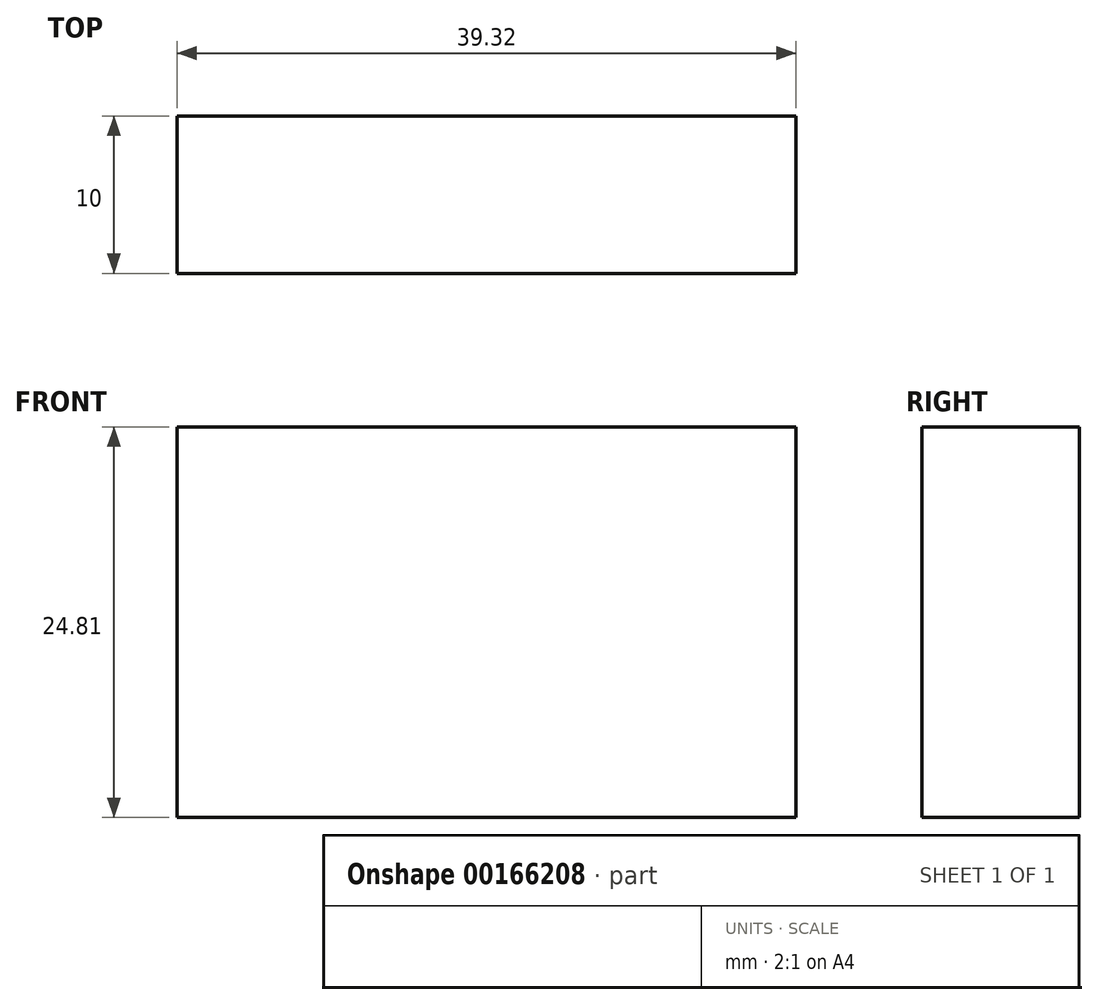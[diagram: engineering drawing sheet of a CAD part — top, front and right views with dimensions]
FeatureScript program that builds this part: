
annotation { "Feature Type Name" : "Feature", "Feature Type Description" : "" }
export const myFeature = defineFeature(function(context is Context, id is Id, definition is map)
    precondition{}
    {
        {
            var Q0;
            Q0=qCreatedBy(makeId("Front.planeOp"),FACE);
            var sketch = newSketch(context, id + "F0", { "sketchPlane" : qUnion([Q0])});
            skLineSegment(sketch, "E0.bottom", {"start": v(0, -2.57) * mm, "end": v(39.32, -2.57) * mm});
            skLineSegment(sketch, "E0.top", {"start": v(0, -27.38) * mm, "end": v(39.32, -27.38) * mm});
            skLineSegment(sketch, "E0.left", {"start": v(0, -2.57) * mm, "end": v(0, -27.38) * mm});
            skLineSegment(sketch, "E0.right", {"start": v(39.32, -2.57) * mm, "end": v(39.32, -27.38) * mm});
            skSolve(sketch);
        }
        {
            var Q0;
            Q0 = qSketchRegion(id + "F0", true);
            extrude(context, id + "F1", {"entities" : qUnion([Q0]), "depth" : 10 * mm});
        }
    });
